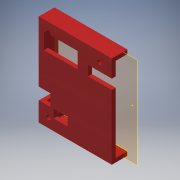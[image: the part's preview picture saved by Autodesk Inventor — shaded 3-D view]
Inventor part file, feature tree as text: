
AUTODESK INVENTOR PART (.ipt)
format: ipt  version: 2017 (Build 210142000, 142)  size: 251,904 bytes
history: native  units: in
note: dims shown in document units (in); Inventor stores cm internally (conversion verified against a paired STEP export)
features: reference x28, sketch x4, other x4, extrude x3, plane x1, chamfer x1
ambient origin geometry x8: Origin, YZ Plane, XZ Plane, XY Plane, X Axis, Y Axis, Z Axis, Center Point
bodies: Solid1 (feature_tree)
feature tree (41):
  plane  "Work Plane1"
  extrude  "Extrusion1"  Depth=0.03in
  extrude  "Extrusion2"  Depth=0.03in
  extrude  "Extrusion3"  Depth=0.03in
  sketch  "Sketch4"  dims[d8=0.03in d9=0.03in d10=0.03in d11=0.03in d12=0.03in d17=0.115in d18=0.115in d19=0.115in d20=0.1in d21=0.0in d22=0.1in d23=0.1in d24=0.1in d25=0.1in d26=0.3in d27=0.0in d28=0.03in d29=0.03in d30=0.03in d31=0.03in d32=0.05in d33=0.015in d34=0.05in d35=0.125in d36=45.0deg]
  chamfer  "Chamfer1"  Distance=0.03in
  sketch  "Sketch1"  dims[d1=0.2in d2=0.0in d3=0.03in]
  reference  "Reference1"
  sketch  "Sketch2"  dims[d4=0.03in d5=0.03in]
  reference  "Reference2"
  reference  "Reference3"
  reference  "Reference4"
  reference  "Reference5"
  reference  "Reference6"
  reference  "Reference7"
  reference  "Reference8"
  reference  "Reference9"
  reference  "Reference10"
  reference  "Reference11"
  reference  "Reference12"
  reference  "Reference13"
  reference  "Reference14"
  reference  "Reference15"
  reference  "Reference16"
  reference  "Reference17"
  reference  "Reference18"
  reference  "Reference19"
  reference  "Reference20"
  reference  "Reference21"
  reference  "Reference22"
  reference  "Reference23"
  reference  "Reference24"
  sketch  "Sketch3"  dims[d6=0.03in d7=0.03in]
  reference  "Reference25"
  reference  "Reference26"
  reference  "Reference27"
  reference  "Reference28"
  other  "<userpath>\Documents\Inventor\PixyCam and Gimbal\Assembly2.iam"
  other  "Assembly2.iam"
  other  "PixyCamKinda:1"
  other  "Assembly1"
